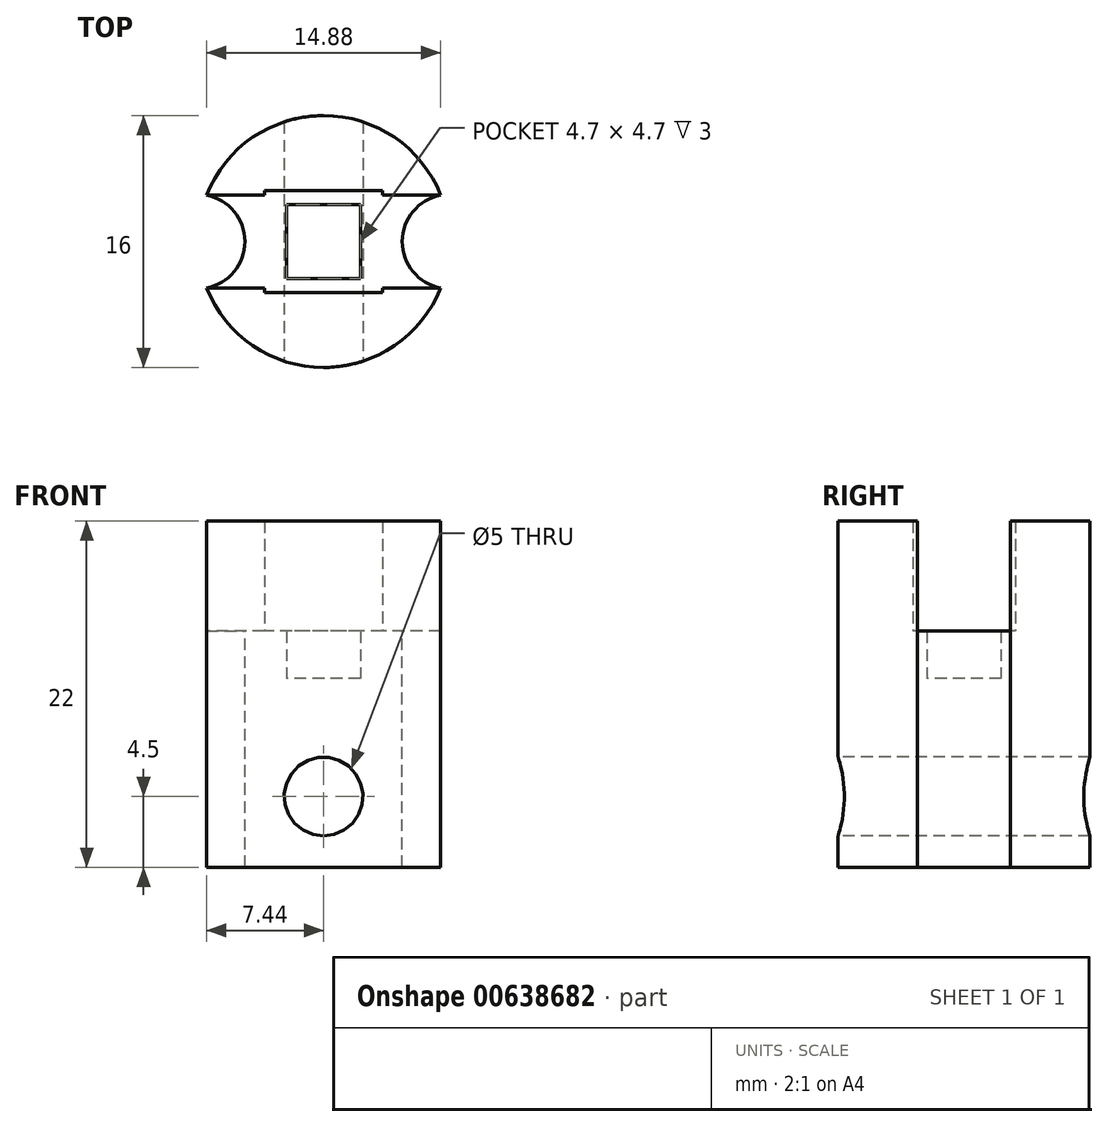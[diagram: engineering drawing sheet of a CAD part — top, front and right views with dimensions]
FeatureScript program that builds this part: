
annotation { "Feature Type Name" : "Feature", "Feature Type Description" : "" }
export const myFeature = defineFeature(function(context is Context, id is Id, definition is map)
    precondition{}
    {
        {
            var Q0;
            Q0=qCreatedBy(makeId("Top.planeOp"),FACE);
            var sketch = newSketch(context, id + "F0", { "sketchPlane" : qUnion([Q0])});
            skCircle(sketch, "E0", {"center": v(0, 0) * mm, "radius": 8 * mm});
            skSolve(sketch);
        }
        {
            var Q0;
            Q0=qSketchRegion(id+"F0",true);
            extrude(context, id + "F1", {"entities" : qUnion([Q0]), "depth" : 3 * mm, "offsetDistance" : 25 * mm});
        }
        {
            var Q0;
            Q0=makeQuery(id+"F1.opExtrude","CAP_FACE",FACE,{"disambiguationData":[OSD([sQuery(id+"F0.wireOp",EDGE,"E0")])],"isStart":true});
            var sketch = newSketch(context, id + "F2", { "sketchPlane" : qUnion([Q0])});
            skCircle(sketch, "E1.0", {"center": v(0, 0) * mm, "radius": 8 * mm});
            skSolve(sketch);
        }
        {
            var Q0;
            Q0=qSketchRegion(id+"F2",true);
            extrude(context, id + "F3", {"entities" : qUnion([Q0]), "operationType" : NewBodyOperationType.ADD, "depth" : 9 * mm, "offsetDistance" : 25 * mm});
        }
        {
            var Q0;
            Q0=makeQuery(id+"F1.opExtrude","CAP_FACE",FACE,{"disambiguationData":[OSD([sQuery(id+"F0.wireOp",EDGE,"E0")])],"isStart":false});
            var sketch = newSketch(context, id + "F4", { "sketchPlane" : qUnion([Q0])});
            skCircle(sketch, "E2", {"center": v(-8, 0) * mm, "radius": 3 * mm});
            skLineSegment(sketch, "E3", {"start": v(0, 0) * mm, "end": v(0, 11.3) * mm, "construction": true});
            skCircle(sketch, "E4.MirrorC", {"center": v(8, 0) * mm, "radius": 3 * mm});
            skSolve(sketch);
        }
        {
            var Q0;
            Q0=qSketchRegion(id+"F4",true);
            extrude(context, id + "F5", {"entities" : qUnion([Q0]), "operationType" : NewBodyOperationType.REMOVE, "endBound" : BoundingType.SYMMETRIC, "oppositeDirection" : true, "depth" : 25 * mm, "offsetDistance" : 25 * mm});
        }
        {
            var Q0;
            Q0=makeQuery(id+"F1.opExtrude","CAP_FACE",FACE,{"disambiguationData":[OSD([sQuery(id+"F0.wireOp",EDGE,"E0")])],"isStart":false});
            var sketch = newSketch(context, id + "F6", { "sketchPlane" : qUnion([Q0])});
            skLineSegment(sketch, "E5.bottom", {"start": v(3.75, 3.25) * mm, "end": v(-3.75, 3.25) * mm});
            skLineSegment(sketch, "E5.top", {"start": v(3.75, -3.25) * mm, "end": v(-3.75, -3.25) * mm});
            skLineSegment(sketch, "E5.left", {"start": v(3.75, 3.25) * mm, "end": v(3.75, 2.95) * mm});
            skLineSegment(sketch, "E5.right", {"start": v(-3.75, 3.25) * mm, "end": v(-3.75, 2.95) * mm});
            skPoint(sketch, "E5.middle", {"position": v(0, 0) * mm});
            skArc(sketch, "E6.0", {"start": v(7.44, 2.95) * mm, "mid": v(0, 8) * mm, "end": v(-7.44, 2.95) * mm});
            skArc(sketch, "E7.0", {"start": v(-7.44, -2.95) * mm, "mid": v(0, -8) * mm, "end": v(7.44, -2.95) * mm});
            skLineSegment(sketch, "E8.bottom", {"start": v(7.44, 2.95) * mm, "end": v(3.75, 2.95) * mm});
            skLineSegment(sketch, "E8.top", {"start": v(7.44, -2.95) * mm, "end": v(3.75, -2.95) * mm});
            skLineSegment(sketch, "E8.left", {"start": v(7.44, 2.95) * mm, "end": v(7.44, -2.95) * mm});
            skLineSegment(sketch, "E9.trimOffspring", {"start": v(-3.75, 2.95) * mm, "end": v(-7.44, 2.95) * mm});
            skLineSegment(sketch, "E10.trimOffspring", {"start": v(-3.75, -2.95) * mm, "end": v(-3.75, -3.25) * mm});
            skLineSegment(sketch, "E11.trimOffspring", {"start": v(-3.75, -2.95) * mm, "end": v(-7.44, -2.95) * mm});
            skLineSegment(sketch, "E12.trimOffspring", {"start": v(3.75, -2.95) * mm, "end": v(3.75, -3.25) * mm});
            skSolve(sketch);
        }
        {
            var Q0;
            Q0=qSketchRegion(id+"F6",true);
            extrude(context, id + "F7", {"entities" : qUnion([Q0]), "operationType" : NewBodyOperationType.ADD, "depth" : 10 * mm, "offsetDistance" : 25 * mm});
        }
        {
            var Q0;
            Q0=makeQuery(id+"F1.opExtrude","CAP_FACE",FACE,{"disambiguationData":[OSD([sQuery(id+"F0.wireOp",EDGE,"E0")])],"isStart":false});
            var sketch = newSketch(context, id + "F8", { "sketchPlane" : qUnion([Q0])});
            skLineSegment(sketch, "E13.bottom", {"start": v(2.35, 2.35) * mm, "end": v(-2.35, 2.35) * mm});
            skLineSegment(sketch, "E13.top", {"start": v(2.35, -2.35) * mm, "end": v(-2.35, -2.35) * mm});
            skLineSegment(sketch, "E13.left", {"start": v(2.35, 2.35) * mm, "end": v(2.35, -2.35) * mm});
            skLineSegment(sketch, "E13.right", {"start": v(-2.35, 2.35) * mm, "end": v(-2.35, -2.35) * mm});
            skPoint(sketch, "E13.middle", {"position": v(0, 0) * mm});
            skArc(sketch, "E14.0", {"start": v(-7.44, -2.95) * mm, "mid": v(-5, 0) * mm, "end": v(-7.44, 2.95) * mm});
            skLineSegment(sketch, "E15.0", {"start": v(-3.75, 2.95) * mm, "end": v(-7.44, 2.95) * mm});
            skLineSegment(sketch, "E16.0", {"start": v(-3.75, 3.25) * mm, "end": v(-3.75, 2.95) * mm});
            skLineSegment(sketch, "E17.0", {"start": v(3.75, 3.25) * mm, "end": v(-3.75, 3.25) * mm});
            skLineSegment(sketch, "E18.0", {"start": v(3.75, 3.25) * mm, "end": v(3.75, 2.95) * mm});
            skLineSegment(sketch, "E19.0", {"start": v(7.44, 2.95) * mm, "end": v(3.75, 2.95) * mm});
            skArc(sketch, "E20.0", {"start": v(7.44, -2.95) * mm, "mid": v(5, 0) * mm, "end": v(7.44, 2.95) * mm});
            skLineSegment(sketch, "E21.0", {"start": v(7.44, -2.95) * mm, "end": v(3.75, -2.95) * mm});
            skLineSegment(sketch, "E22.0", {"start": v(3.75, -2.95) * mm, "end": v(3.75, -3.25) * mm});
            skLineSegment(sketch, "E23.0", {"start": v(3.75, -3.25) * mm, "end": v(-3.75, -3.25) * mm});
            skLineSegment(sketch, "E24.0", {"start": v(-3.75, -2.95) * mm, "end": v(-3.75, -3.25) * mm});
            skLineSegment(sketch, "E25.0", {"start": v(-3.75, -2.95) * mm, "end": v(-7.44, -2.95) * mm});
            skSolve(sketch);
        }
        {
            var Q0;
            Q0=qSketchRegion(id+"F8",true);
            extrude(context, id + "F9", {"entities" : qUnion([Q0]), "operationType" : NewBodyOperationType.ADD, "depth" : 3 * mm, "offsetDistance" : 25 * mm});
        }
        {
            var Q0;
            Q0=qCreatedBy(makeId("Front.planeOp"),FACE);
            var sketch = newSketch(context, id + "F10", { "sketchPlane" : qUnion([Q0])});
            skCircle(sketch, "E26", {"center": v(0, -4.5) * mm, "radius": 2.5 * mm});
            skLineSegment(sketch, "E27.0", {"start": v(7.44, -9) * mm, "end": v(-7.44, -9) * mm, "construction": true});
            skLineSegment(sketch, "E28", {"start": v(0, 0) * mm, "end": v(0, -9) * mm, "construction": true});
            skSolve(sketch);
        }
        {
            var Q0;
            Q0 = qSketchRegion(id + "F10", true);
            extrude(context, id + "F11", {"entities" : qUnion([Q0]), "operationType" : NewBodyOperationType.REMOVE, "endBound" : BoundingType.THROUGH_ALL, "oppositeDirection" : true, "depth" : 25 * mm, "offsetDistance" : 25 * mm, "hasSecondDirection" : true, "secondDirectionOppositeDirection" : false, "secondDirectionDepth" : 25 * mm});
        }
    });
